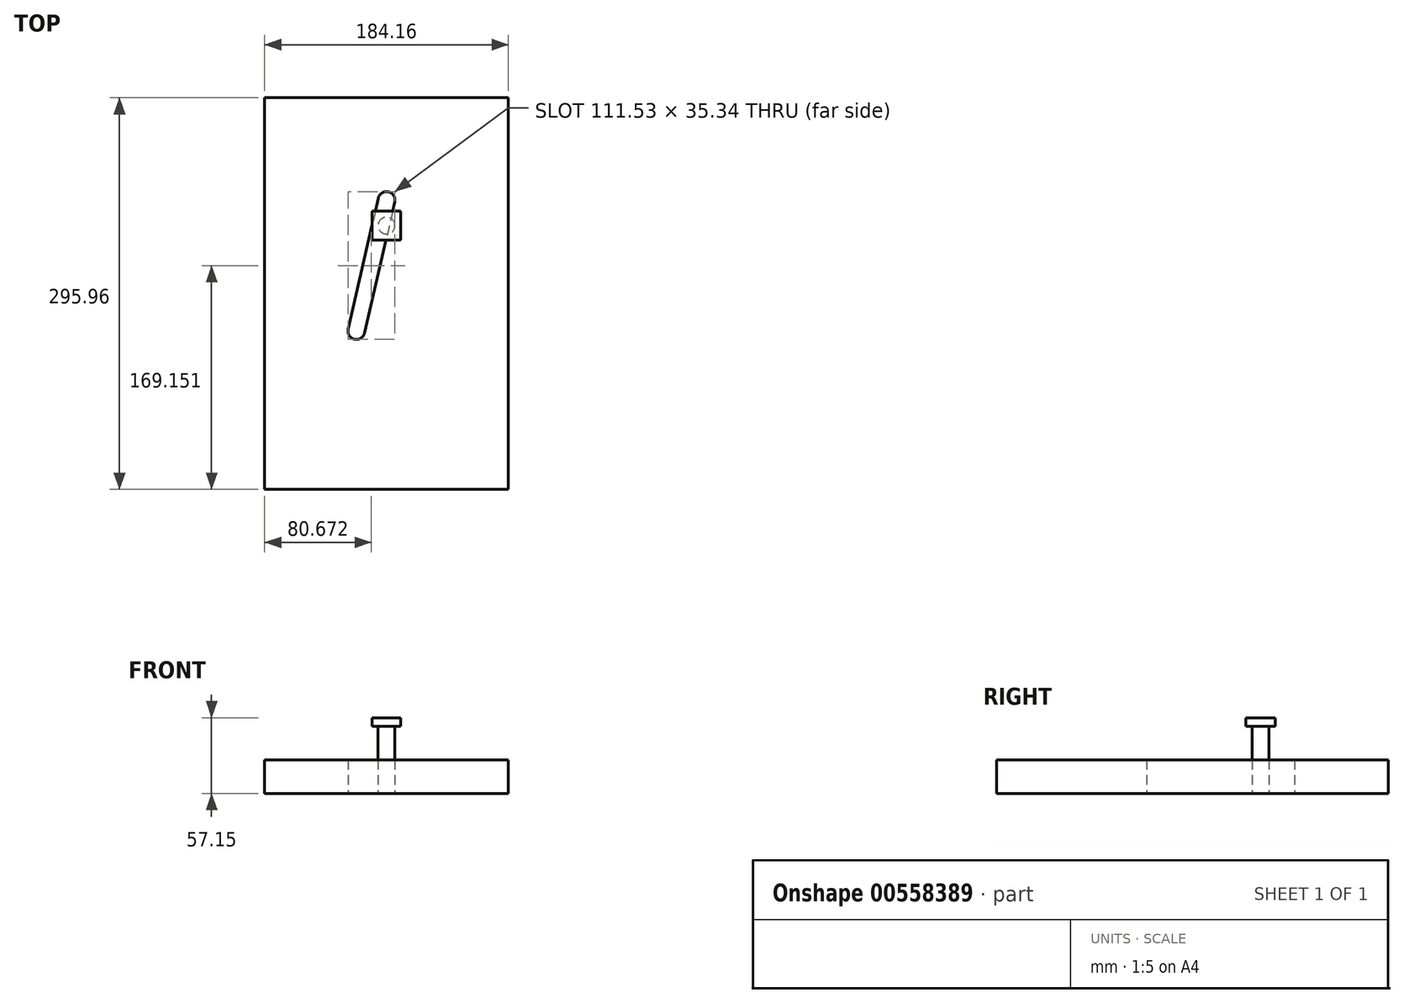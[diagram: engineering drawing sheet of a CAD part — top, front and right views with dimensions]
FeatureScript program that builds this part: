
annotation { "Feature Type Name" : "Feature", "Feature Type Description" : "" }
export const myFeature = defineFeature(function(context is Context, id is Id, definition is map)
    precondition{}
    {
        {
            var Q0;
            Q0=qCreatedBy(makeId("Top.planeOp"),FACE);
            var sketch = newSketch(context, id + "F0", { "sketchPlane" : qUnion([Q0])});
            skLineSegment(sketch, "E0.bottom", {"start": v(-92.08, -147.98) * mm, "end": v(92.08, -147.98) * mm});
            skLineSegment(sketch, "E0.top", {"start": v(-92.08, 147.98) * mm, "end": v(92.08, 147.98) * mm});
            skLineSegment(sketch, "E0.left", {"start": v(-92.08, -147.98) * mm, "end": v(-92.08, 147.98) * mm});
            skLineSegment(sketch, "E0.right", {"start": v(92.08, -147.98) * mm, "end": v(92.08, 147.98) * mm});
            skPoint(sketch, "E0.middle", {"position": v(0, 0) * mm});
            skLineSegment(sketch, "E1", {"start": v(0, 70.67) * mm, "end": v(-22.81, -28.33) * mm});
            skArc(sketch, "E2.0.startCap", {"start": v(-6.19, 72.1) * mm, "mid": v(1.43, 76.86) * mm, "end": v(6.19, 69.25) * mm});
            skArc(sketch, "E2.0.endCap", {"start": v(-16.63, -29.76) * mm, "mid": v(-24.24, -34.52) * mm, "end": v(-29, -26.9) * mm});
            skLineSegment(sketch, "E2.0.left", {"start": v(6.19, 69.25) * mm, "end": v(-16.63, -29.76) * mm});
            skLineSegment(sketch, "E2.0.right", {"start": v(-6.19, 72.1) * mm, "end": v(-29, -26.9) * mm});
            skSolve(sketch);
        }
        {
            var Q0;
            Q0 = qSketchRegion(id + "F0", true);
            extrude(context, id + "F1", {"entities" : qUnion([Q0]), "depth" : 25.4 * mm, "offsetDistance" : 25.4 * mm});
        }
        {
            var Q0;
            Q0=qCreatedBy(makeId("Top.planeOp"),FACE);
            var sketch = newSketch(context, id + "F2", { "sketchPlane" : qUnion([Q0])});
            skCircle(sketch, "E3", {"center": v(0, 51.37) * mm, "radius": 6.35 * mm});
            skSolve(sketch);
        }
        {
            var Q0;
            Q0 = qSketchRegion(id + "F2", true);
            extrude(context, id + "F3", {"entities" : qUnion([Q0]), "depth" : 50.8 * mm, "offsetDistance" : 25.4 * mm});
        }
        {
            var Q0;
            Q0=makeQuery(id+"F3.opExtrude","CAP_FACE",FACE,{"disambiguationData":[OSD([sQuery(id+"F2.wireOp",EDGE,"E3")])],"isStart":false});
            var sketch = newSketch(context, id + "F4", { "sketchPlane" : qUnion([Q0])});
            skLineSegment(sketch, "E4.bottom", {"start": v(-10.76, 40.31) * mm, "end": v(10.76, 40.31) * mm});
            skLineSegment(sketch, "E4.top", {"start": v(-10.76, 62.43) * mm, "end": v(10.76, 62.43) * mm});
            skLineSegment(sketch, "E4.left", {"start": v(-10.76, 40.31) * mm, "end": v(-10.76, 62.43) * mm});
            skLineSegment(sketch, "E4.right", {"start": v(10.76, 40.31) * mm, "end": v(10.76, 62.43) * mm});
            skPoint(sketch, "E4.middle", {"position": v(0, 51.37) * mm});
            skSolve(sketch);
        }
        {
            var Q0;
            Q0 = qSketchRegion(id + "F4", true);
            extrude(context, id + "F5", {"entities" : qUnion([Q0]), "operationType" : NewBodyOperationType.ADD, "depth" : 6.35 * mm, "offsetDistance" : 25.4 * mm});
        }
    });
